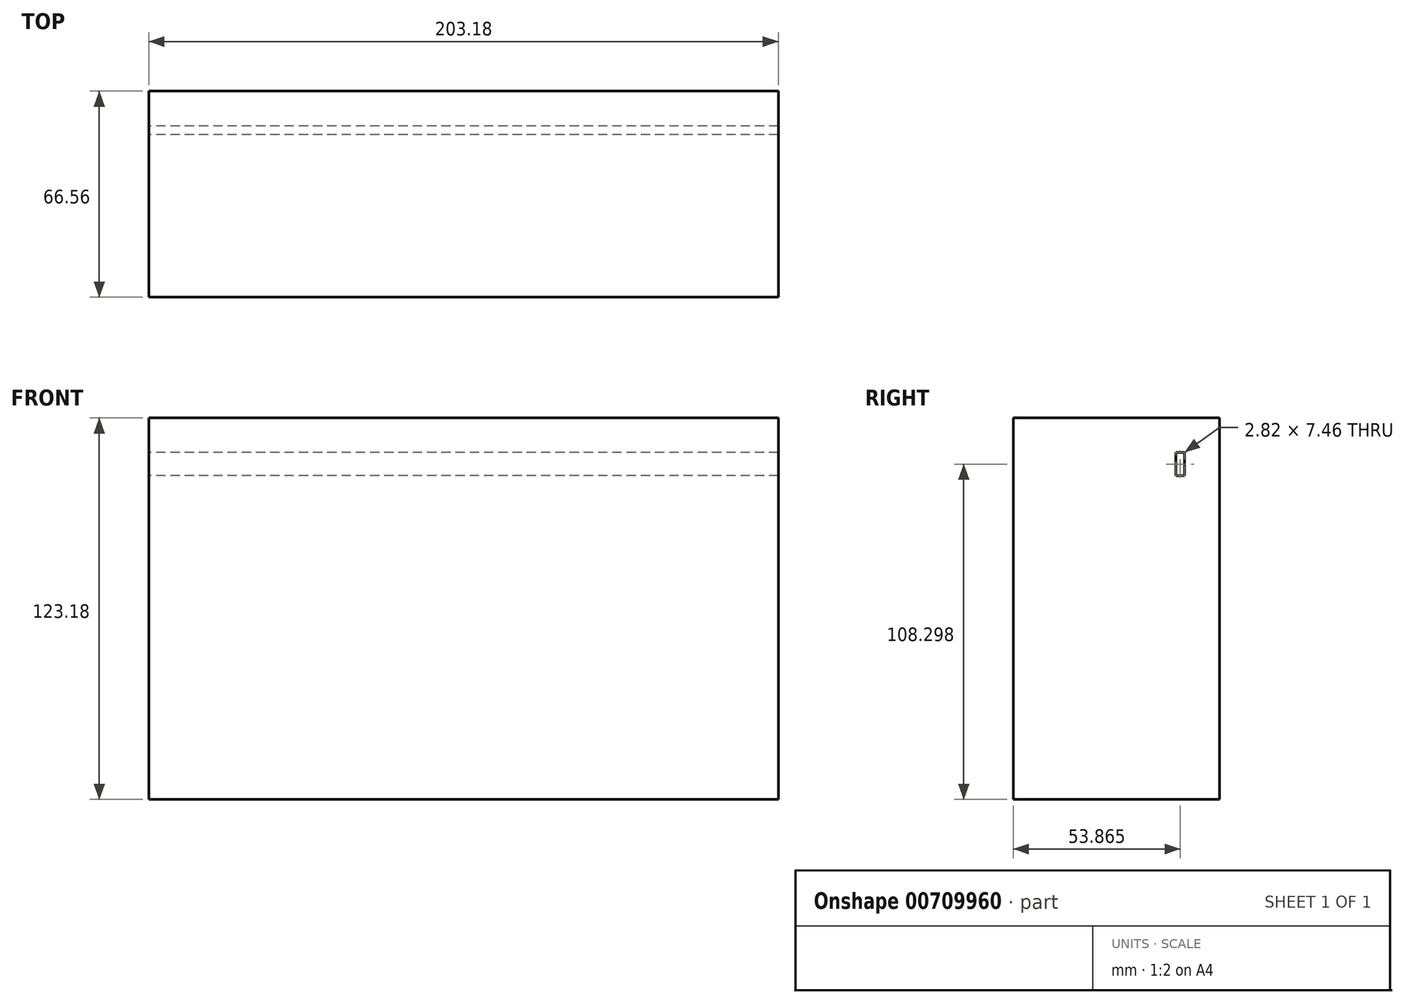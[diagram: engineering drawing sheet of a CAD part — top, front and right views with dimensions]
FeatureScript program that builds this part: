
annotation { "Feature Type Name" : "Feature", "Feature Type Description" : "" }
export const myFeature = defineFeature(function(context is Context, id is Id, definition is map)
    precondition{}
    {
        {
            var Q0;
            Q0=qCreatedBy(makeId("Right.planeOp"),FACE);
            var sketch = newSketch(context, id + "F0", { "sketchPlane" : qUnion([Q0])});
            skLineSegment(sketch, "E0.bottom", {"start": v(43.34, -82.73) * mm, "end": v(109.9, -82.73) * mm});
            skLineSegment(sketch, "E0.top", {"start": v(43.34, 40.45) * mm, "end": v(109.9, 40.45) * mm});
            skLineSegment(sketch, "E0.left", {"start": v(43.34, -82.73) * mm, "end": v(43.34, 40.45) * mm});
            skLineSegment(sketch, "E0.right", {"start": v(109.9, -82.73) * mm, "end": v(109.9, 40.45) * mm});
            skLineSegment(sketch, "E1.bottom", {"start": v(95.8, 21.84) * mm, "end": v(98.62, 21.84) * mm});
            skLineSegment(sketch, "E1.top", {"start": v(95.8, 29.3) * mm, "end": v(98.62, 29.3) * mm});
            skLineSegment(sketch, "E1.left", {"start": v(95.8, 21.84) * mm, "end": v(95.8, 29.3) * mm});
            skLineSegment(sketch, "E1.right", {"start": v(98.62, 21.84) * mm, "end": v(98.62, 29.3) * mm});
            skSolve(sketch);
        }
        {
            var Q0;
            Q0=makeQuery(id+"F0.imprint","IMPRINT",FACE,{"disambiguationData":[TD([[makeQuery(id+"F0.imprint","IMPRINT",EDGE,{"derivedFrom":sQuery(id+"F0.wireOp",EDGE,"E0.bottom")}),1.0]])]});
            extrude(context, id + "F1", {"entities" : qUnion([Q0]), "depth" : 203.18 * mm, "offsetDistance" : 25.4 * mm});
        }
    });
